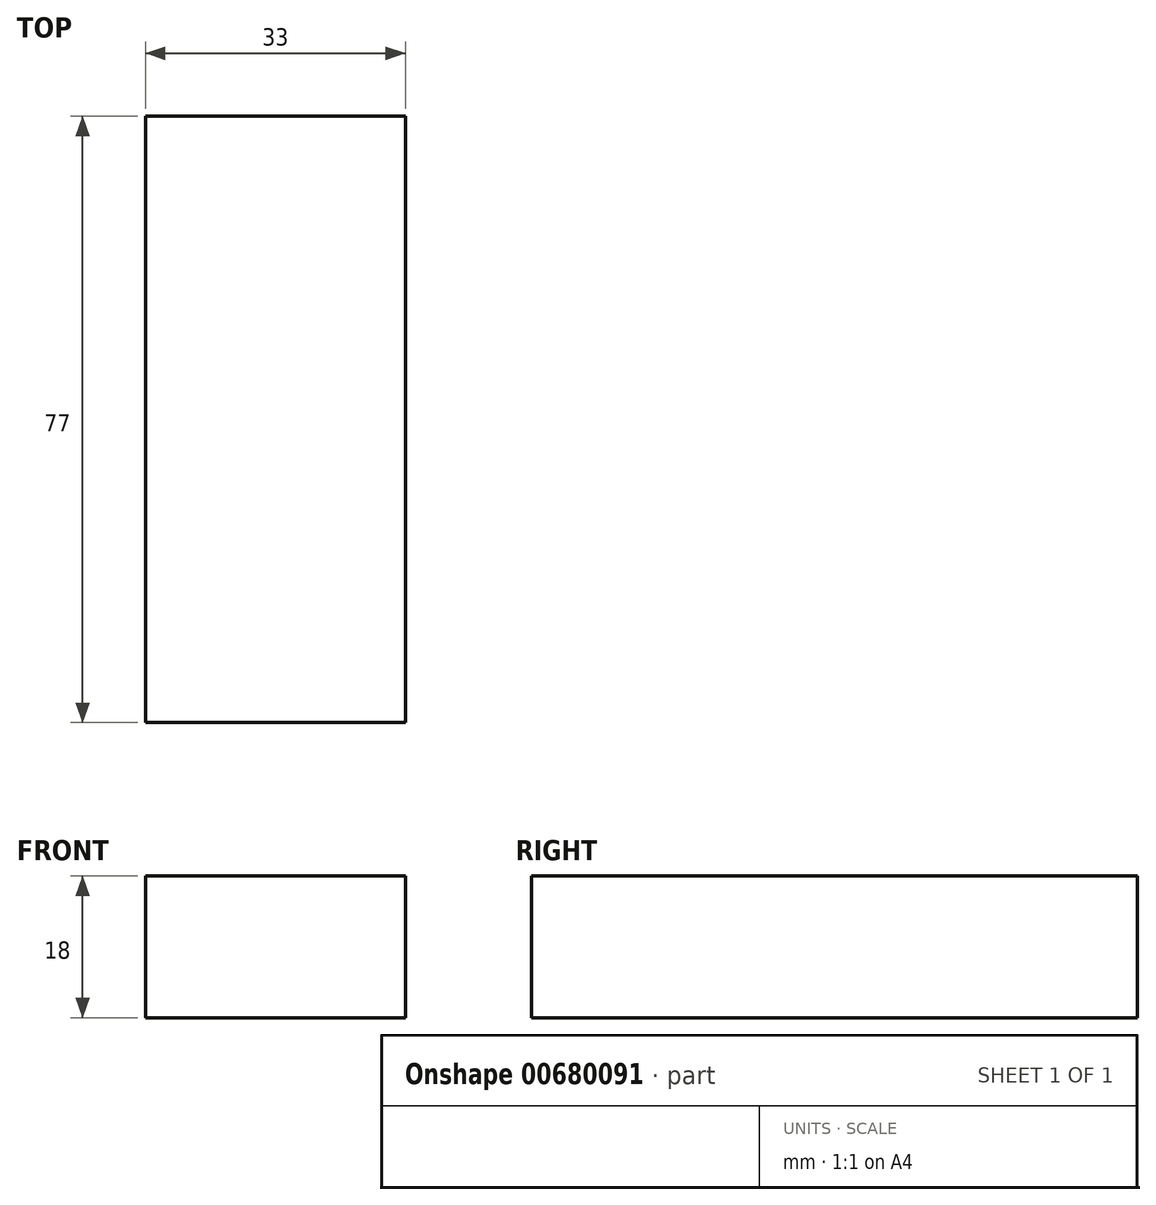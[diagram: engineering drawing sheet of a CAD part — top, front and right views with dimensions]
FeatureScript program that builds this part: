
annotation { "Feature Type Name" : "Feature", "Feature Type Description" : "" }
export const myFeature = defineFeature(function(context is Context, id is Id, definition is map)
    precondition{}
    {
        {
            var Q0;
            Q0=qCreatedBy(makeId("Top.planeOp"),FACE);
            var sketch = newSketch(context, id + "F0", { "sketchPlane" : qUnion([Q0])});
            skLineSegment(sketch, "E0.bottom", {"start": v(16.5, -38.5) * mm, "end": v(-16.5, -38.5) * mm});
            skLineSegment(sketch, "E0.top", {"start": v(16.5, 38.5) * mm, "end": v(-16.5, 38.5) * mm});
            skLineSegment(sketch, "E0.left", {"start": v(16.5, -38.5) * mm, "end": v(16.5, 38.5) * mm});
            skLineSegment(sketch, "E0.right", {"start": v(-16.5, -38.5) * mm, "end": v(-16.5, 38.5) * mm});
            skPoint(sketch, "E0.middle", {"position": v(0, 0) * mm});
            skSolve(sketch);
        }
        {
            var Q0;
            Q0=makeQuery(id+"F0.imprint","IMPRINT",FACE,{"disambiguationData":[TD([[makeQuery(id+"F0.imprint","IMPRINT",EDGE,{"derivedFrom":sQuery(id+"F0.wireOp",EDGE,"E0.bottom")}),-1.0]])]});
            extrude(context, id + "F1", {"entities" : qUnion([Q0]), "depth" : 18 * mm, "offsetDistance" : 25.4 * mm});
        }
    });
